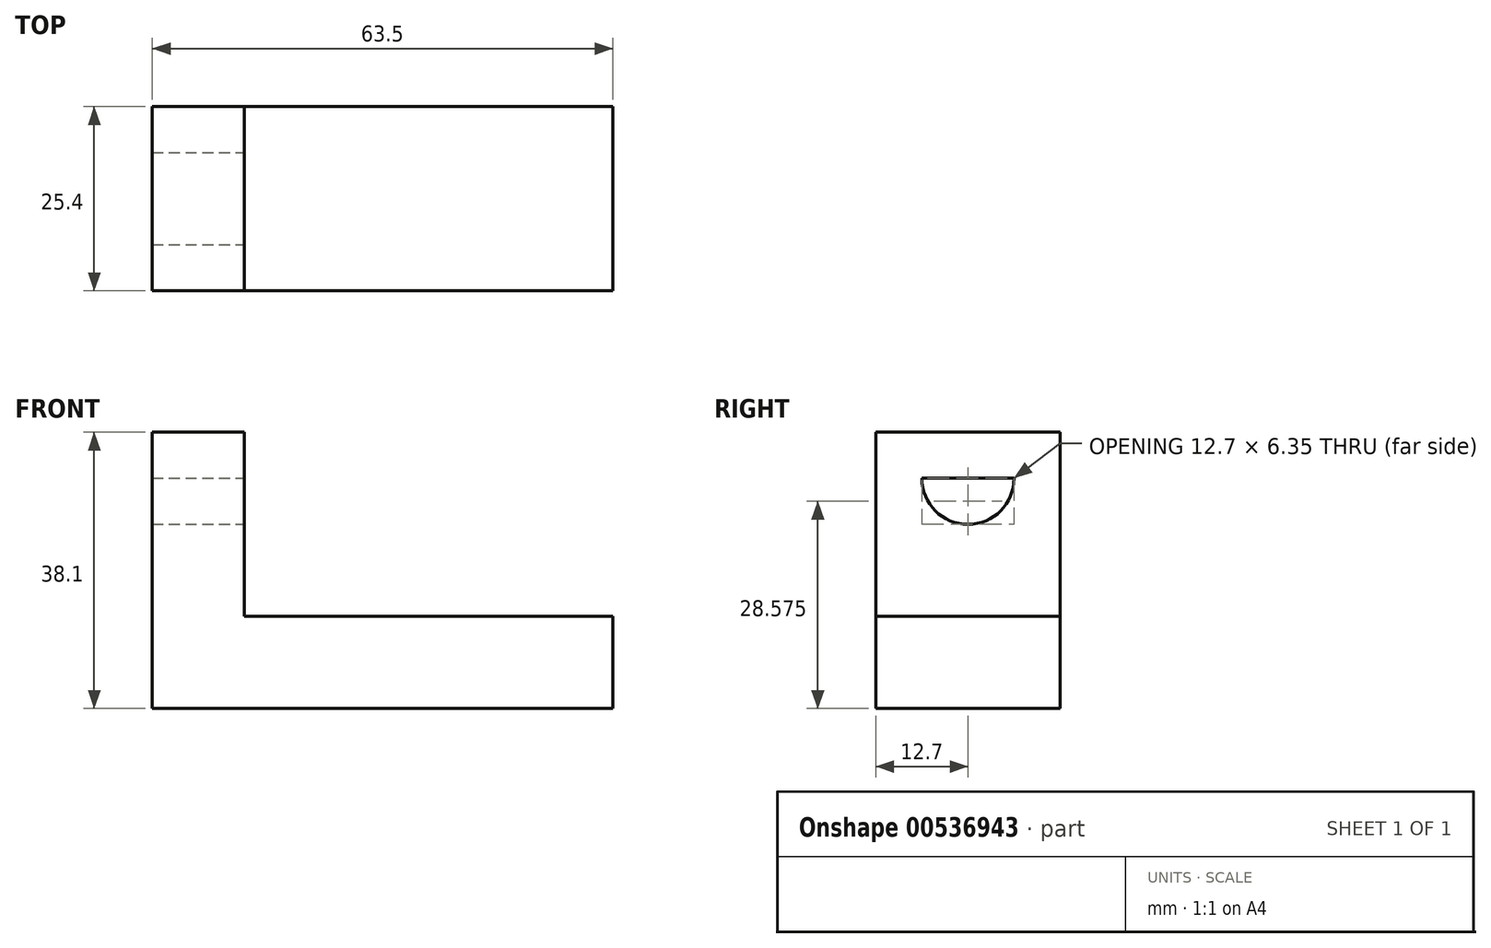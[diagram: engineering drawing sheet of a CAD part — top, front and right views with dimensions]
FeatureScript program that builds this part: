
annotation { "Feature Type Name" : "Feature", "Feature Type Description" : "" }
export const myFeature = defineFeature(function(context is Context, id is Id, definition is map)
    precondition{}
    {
        {
            var Q0;
            Q0=qCreatedBy(makeId("Front.planeOp"),FACE);
            var sketch = newSketch(context, id + "F0", { "sketchPlane" : qUnion([Q0])});
            skLineSegment(sketch, "E0.bottom", {"start": v(-37.51, 0) * mm, "end": v(25.99, 0) * mm});
            skLineSegment(sketch, "E0.top", {"start": v(-37.51, 12.7) * mm, "end": v(25.99, 12.7) * mm});
            skLineSegment(sketch, "E0.left", {"start": v(-37.51, 0) * mm, "end": v(-37.51, 12.7) * mm});
            skLineSegment(sketch, "E0.right", {"start": v(25.99, 0) * mm, "end": v(25.99, 12.7) * mm});
            skLineSegment(sketch, "E1", {"start": v(-37.51, 12.7) * mm, "end": v(-37.51, 38.1) * mm});
            skLineSegment(sketch, "E2", {"start": v(-37.51, 38.1) * mm, "end": v(-24.81, 38.1) * mm});
            skLineSegment(sketch, "E3", {"start": v(-24.81, 38.1) * mm, "end": v(-24.81, 12.7) * mm});
            skLineSegment(sketch, "E4", {"start": v(-24.81, 12.7) * mm, "end": v(-37.51, 12.7) * mm});
            skSolve(sketch);
        }
        {
            var Q0;
            Q0 = qSketchRegion(id + "F0", true);
            extrude(context, id + "F1", {"entities" : qUnion([Q0]), "depth" : 25.4 * mm, "offsetDistance" : 25.4 * mm});
        }
        {
            var Q0;
            Q0 = qSketchRegion(id + "F0", true);
            extrude(context, id + "F2", {"entities" : qUnion([Q0]), "operationType" : NewBodyOperationType.ADD, "depth" : 25.4 * mm, "offsetDistance" : 25.4 * mm});
        }
        {
            var Q0;
            Q0=makeQuery(id+"F1.opExtrude","SWEPT_FACE",FACE,{"disambiguationData":[OSD([sQuery(id+"F0.wireOp",EDGE,"E3")])]});
            var sketch = newSketch(context, id + "F3", { "sketchPlane" : qUnion([Q0])});
            skLineSegment(sketch, "E5", {"start": v(-19.05, 38.1) * mm, "end": v(-19.05, 31.75) * mm});
            skLineSegment(sketch, "E6", {"start": v(-19.05, 31.75) * mm, "end": v(-19.05, 38.1) * mm});
            skLineSegment(sketch, "E7", {"start": v(-6.35, 38.1) * mm, "end": v(-6.35, 31.75) * mm});
            skLineSegment(sketch, "E8", {"start": v(-6.35, 31.75) * mm, "end": v(-19.05, 31.75) * mm});
            skArc(sketch, "E9", {"start": v(-19.05, 31.75) * mm, "mid": v(-12.7, 25.4) * mm, "end": v(-6.35, 31.75) * mm});
            skSolve(sketch);
        }
        {
            var Q0;
            Q0 = qSketchRegion(id + "F3", true);
            var Q1;
            {var subQ0=sQuery(id+"F3.wireOp",EDGE,"E6");Q1=makeQuery(id+"F3.imprint","IMPRINT",FACE,{"disambiguationData":[TD([[makeQuery(id+"F3.imprint","IMPRINT",EDGE,{"derivedFrom":subQ0}),-1.0]])]});}
            extrude(context, id + "F4", {"entities" : qUnion([Q0, Q1]), "operationType" : NewBodyOperationType.REMOVE, "oppositeDirection" : true, "depth" : 25.4 * mm, "offsetDistance" : 25.4 * mm});
        }
    });
